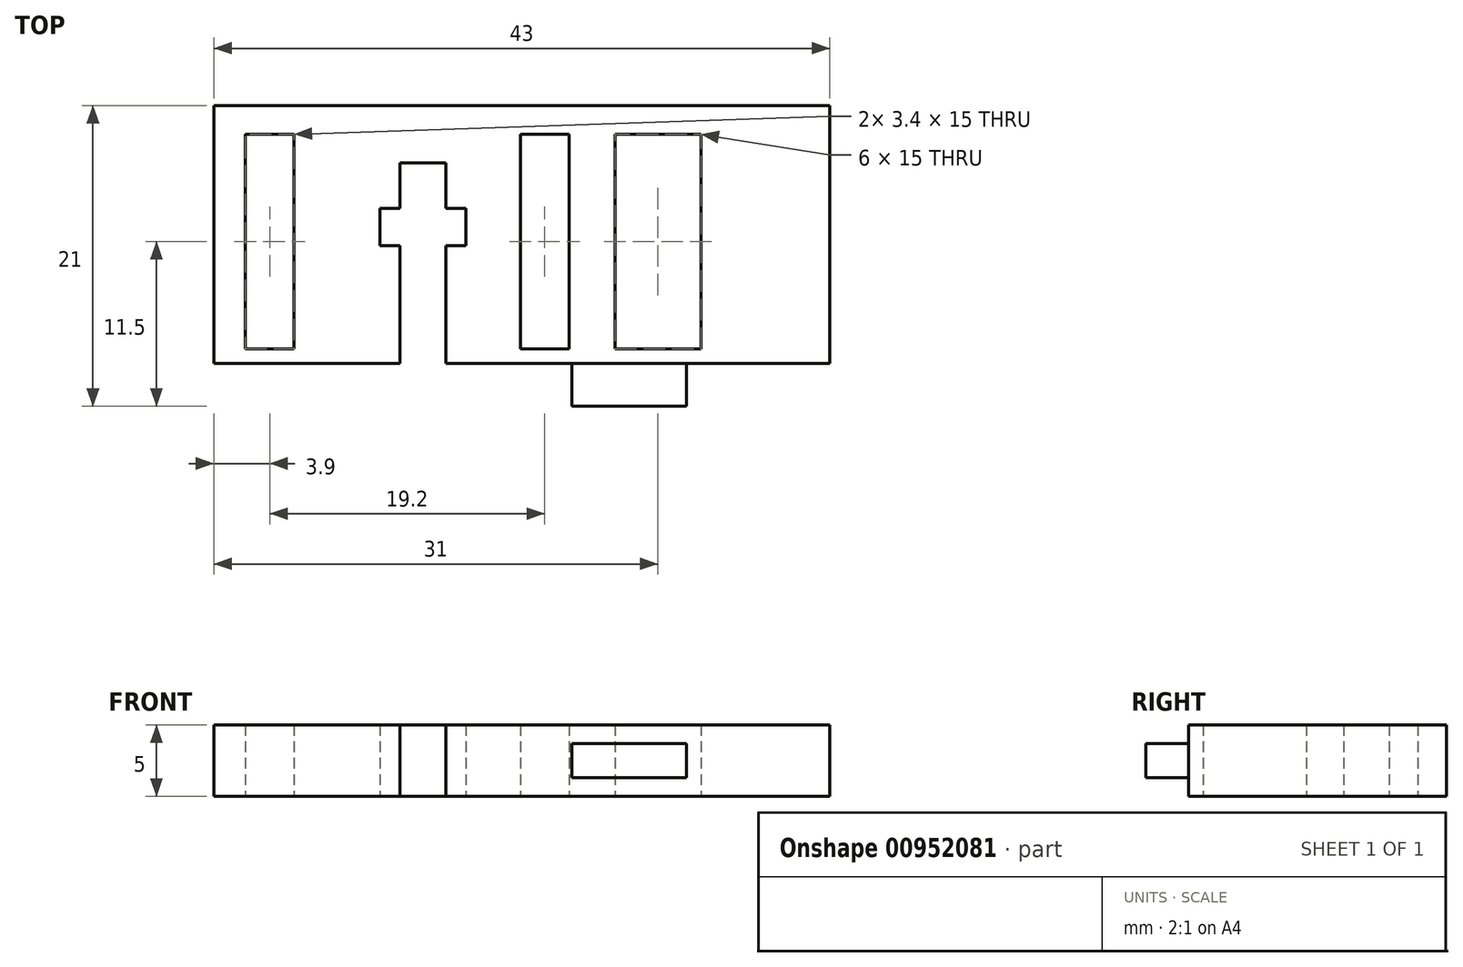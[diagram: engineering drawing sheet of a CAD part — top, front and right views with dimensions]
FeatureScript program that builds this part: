
annotation { "Feature Type Name" : "Feature", "Feature Type Description" : "" }
export const myFeature = defineFeature(function(context is Context, id is Id, definition is map)
    precondition{}
    {
        {
            var Q0;
            Q0=qCreatedBy(makeId("Top.planeOp"),FACE);
            var sketch = newSketch(context, id + "F0", { "sketchPlane" : qUnion([Q0])});
            skLineSegment(sketch, "E0.bottom", {"start": v(0, 0) * mm, "end": v(43, 0) * mm});
            skLineSegment(sketch, "E0.top", {"start": v(0, -18) * mm, "end": v(43, -18) * mm});
            skLineSegment(sketch, "E0.left", {"start": v(0, 0) * mm, "end": v(0, -18) * mm});
            skLineSegment(sketch, "E0.right", {"start": v(43, 0) * mm, "end": v(43, -18) * mm});
            skLineSegment(sketch, "E1.bottom", {"start": v(2.2, -2) * mm, "end": v(5.6, -2) * mm});
            skLineSegment(sketch, "E1.top", {"start": v(2.2, -17) * mm, "end": v(5.6, -17) * mm});
            skLineSegment(sketch, "E1.left", {"start": v(2.2, -2) * mm, "end": v(2.2, -17) * mm});
            skLineSegment(sketch, "E1.right", {"start": v(5.6, -2) * mm, "end": v(5.6, -17) * mm});
            skLineSegment(sketch, "E2.bottom", {"start": v(21.4, -2) * mm, "end": v(24.8, -2) * mm});
            skLineSegment(sketch, "E2.top", {"start": v(21.4, -17) * mm, "end": v(24.8, -17) * mm});
            skLineSegment(sketch, "E2.left", {"start": v(21.4, -2) * mm, "end": v(21.4, -17) * mm});
            skLineSegment(sketch, "E2.right", {"start": v(24.8, -2) * mm, "end": v(24.8, -17) * mm});
            skLineSegment(sketch, "E3.bottom", {"start": v(13, -18) * mm, "end": v(16.2, -18) * mm});
            skLineSegment(sketch, "E3.top", {"start": v(13, -4) * mm, "end": v(16.2, -4) * mm});
            skLineSegment(sketch, "E3.left", {"start": v(13, -18) * mm, "end": v(13, -4) * mm});
            skLineSegment(sketch, "E3.right", {"start": v(16.2, -18) * mm, "end": v(16.2, -4) * mm});
            skLineSegment(sketch, "E4.bottom", {"start": v(28, -2) * mm, "end": v(34, -2) * mm});
            skLineSegment(sketch, "E4.top", {"start": v(28, -17) * mm, "end": v(34, -17) * mm});
            skLineSegment(sketch, "E4.left", {"start": v(28, -2) * mm, "end": v(28, -17) * mm});
            skLineSegment(sketch, "E4.right", {"start": v(34, -2) * mm, "end": v(34, -17) * mm});
            skLineSegment(sketch, "E5.bottom", {"start": v(11.6, -7.2) * mm, "end": v(17.6, -7.2) * mm});
            skLineSegment(sketch, "E5.top", {"start": v(11.6, -9.8) * mm, "end": v(17.6, -9.8) * mm});
            skLineSegment(sketch, "E5.left", {"start": v(11.6, -7.2) * mm, "end": v(11.6, -9.8) * mm});
            skLineSegment(sketch, "E5.right", {"start": v(17.6, -7.2) * mm, "end": v(17.6, -9.8) * mm});
            skSolve(sketch);
        }
        {
            var Q0;
            Q0=makeQuery(id+"F0.imprint","IMPRINT",FACE,{"disambiguationData":[TD([[makeQuery(id+"F0.imprint","IMPRINT",EDGE,{"derivedFrom":sQuery(id+"F0.wireOp",EDGE,"E0.bottom")}),-1.0]])]});
            extrude(context, id + "F1", {"entities" : qUnion([Q0]), "depth" : 2.5 * mm, "offsetDistance" : 25 * mm, "hasSecondDirection" : true, "secondDirectionOppositeDirection" : true, "secondDirectionDepth" : 2.5 * mm});
        }
        {
            var Q0;
            {var subQ0=sQuery(id+"F0.wireOp",EDGE,"E0.top");Q0=makeQuery(id+"F1.opExtrude","SWEPT_FACE",FACE,{"disambiguationData":[OSD([subQ0]),TDD([makeQuery(id+"F0.imprint","IMPRINT",EDGE,{"disambiguationData":[TD([[makeQuery(id+"F0.imprint","INTERSECT",VERTEX,{"derivedFrom":[subQ0,sQuery(id+"F0.wireOp",EDGE,"E3.right")]}),-1.0]])],"derivedFrom":subQ0})])]});}
            var sketch = newSketch(context, id + "F2", { "sketchPlane" : qUnion([Q0])});
            skLineSegment(sketch, "E6.bottom", {"start": v(33, 0) * mm, "end": v(25, 0) * mm});
            skLineSegment(sketch, "E6.top", {"start": v(33, 1.2) * mm, "end": v(25, 1.2) * mm});
            skLineSegment(sketch, "E6.left", {"start": v(25, 0) * mm, "end": v(25, 1.2) * mm});
            skLineSegment(sketch, "E6.right", {"start": v(33, 0) * mm, "end": v(33, 1.2) * mm});
            skLineSegment(sketch, "E7.MirrorCS", {"start": v(33, -1.2) * mm, "end": v(25, -1.2) * mm});
            skLineSegment(sketch, "E8.MirrorCS", {"start": v(25, 0) * mm, "end": v(25, -1.2) * mm});
            skLineSegment(sketch, "E9.MirrorCS", {"start": v(33, 0) * mm, "end": v(33, -1.2) * mm});
            skSolve(sketch);
        }
        {
            var Q0;
            Q0=makeQuery(id+"F2.imprint","IMPRINT",FACE,{"disambiguationData":[TD([[makeQuery(id+"F2.imprint","IMPRINT",EDGE,{"derivedFrom":sQuery(id+"F2.wireOp",EDGE,"E6.bottom")}),-1.0]])]});
            var Q1;
            Q1=makeQuery(id+"F2.imprint","IMPRINT",FACE,{"disambiguationData":[TD([[makeQuery(id+"F2.imprint","IMPRINT",EDGE,{"derivedFrom":sQuery(id+"F2.wireOp",EDGE,"E6.bottom")}),1.0]])]});
            extrude(context, id + "F3", {"entities" : qUnion([Q0, Q1]), "operationType" : NewBodyOperationType.ADD, "depth" : 3 * mm, "offsetDistance" : 25 * mm});
        }
    });
